# Revit family: bimlib_blokirazvetviteli_vp4_sistemamrv-5-rc_haier
name_source: partatom
category: Оборудование
units: mm (PartAtom-declared; Revit-internal decimal feet)

## family parameters
Всегда вертикально = Да
На основе рабочей плоскости = Нет
Общий = Нет
При загрузке вырезать с полостями = Нет
Размер круглого соединителя = Использовать диаметр
Тип детали = Нормальный
Точка расчета площади = Нет

## types (1)
- VP4-450B_HAIER
    ADSK_Версия Revit = 2017
    ADSK_Группирование = VP4 Система MRV 5-RC
    ADSK_Единица измерения = шт.
    ADSK_Завод-изготовитель = Haier Group
    ADSK_Классификация нагрузок = ОВК
    ADSK_Код изделия = VP4-280B
    ADSK_Количество = 1
    ADSK_Количество фаз = 1
    ADSK_Коэффициент мощности = 1
    ADSK_Масса = 18
    ADSK_Наименование = Блоки-разветвители VP4 Система MRV 5-RC (с рекуперацией тепла)
    ADSK_Наименование краткое = VP4 Система MRV 5-RC
    ADSK_Напряжение = 230 В
    ADSK_Номинальная мощность = 45000 Вт
    ADSK_Обозначение = VP4
    ADSK_Полная мощность = 45000 В·А
    ADSK_Размер_Высота = 300 мм
    ADSK_Размер_Глубина = 421 мм
    ADSK_Размер_Ширина = 405 мм
    BL_BIM library = https://bimlib.pro
    HG_URL поставщика = www.haierproff.ru
    URL = www.haier.com
    Диаметр_Газ_ВыскоеДавление_Выход = 22.22 мм
    Диаметр_Газ_Выход = 19.05 мм
    Диаметр_Газ_Подача = 15.88 мм
    Диаметр_Жидкость_Выход = 9.52 мм
    Диаметр_Жидкость_Подача = 9.52 мм
    Изготовитель = Haier Group
    Отметка по умолчанию = 0 мм
    Потребляемая мощность = 45 кВт
    Частота тока = 50 Гц
